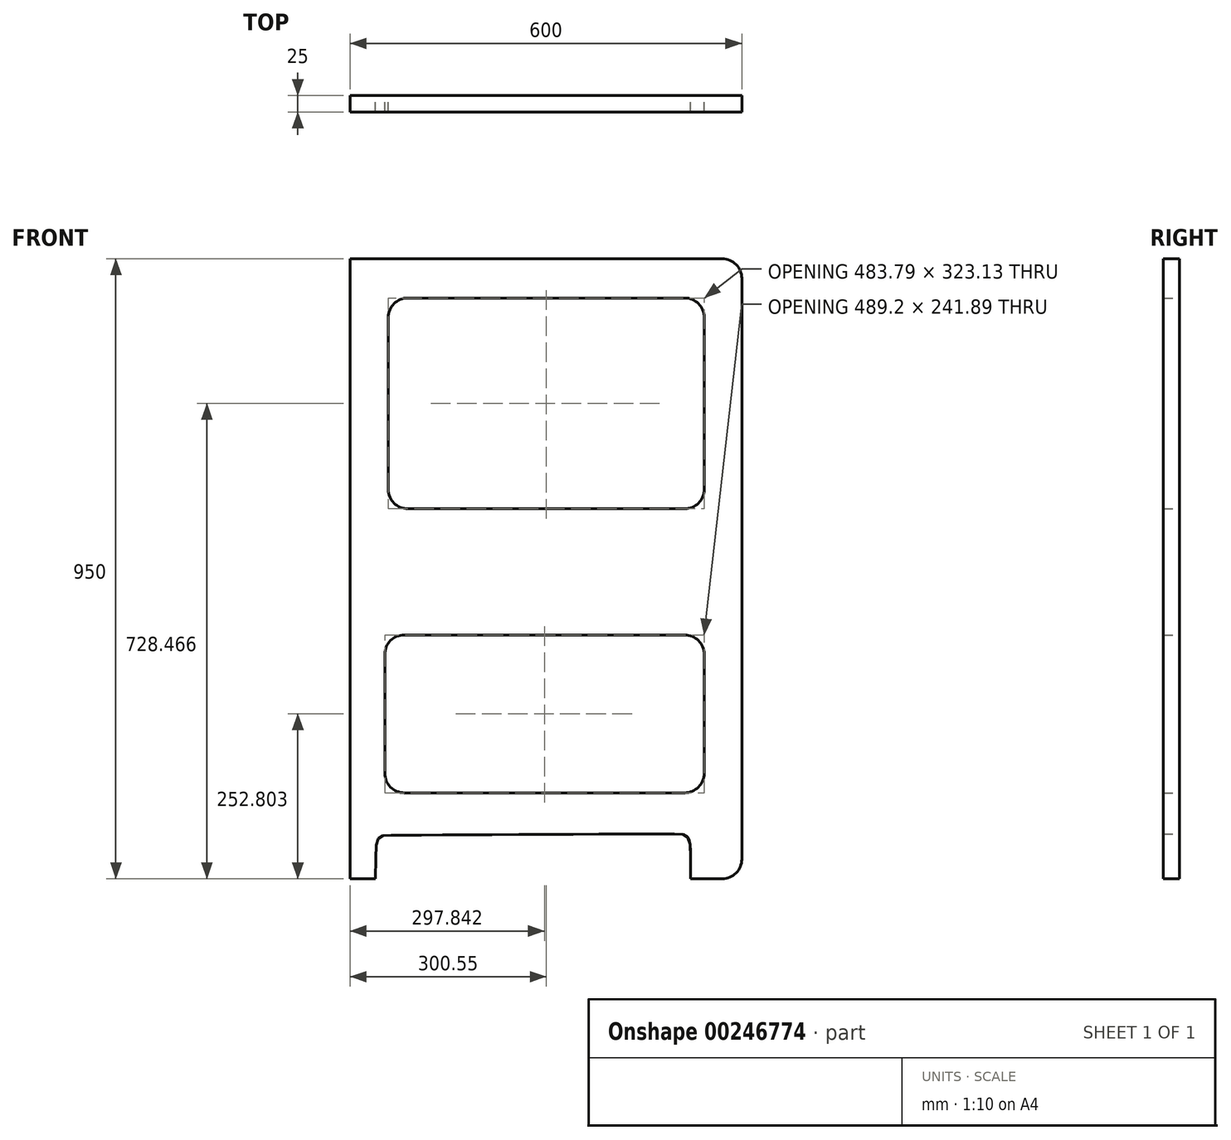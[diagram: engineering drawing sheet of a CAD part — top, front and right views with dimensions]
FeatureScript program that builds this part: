
annotation { "Feature Type Name" : "Feature", "Feature Type Description" : "" }
export const myFeature = defineFeature(function(context is Context, id is Id, definition is map)
    precondition{}
    {
        {
            var Q0;
            Q0=qCreatedBy(makeId("Front.planeOp"),FACE);
            var sketch = newSketch(context, id + "F0", { "sketchPlane" : qUnion([Q0])});
            skLineSegment(sketch, "E0.bottom", {"start": v(-370.61, 491.77) * mm, "end": v(199.39, 491.77) * mm});
            skLineSegment(sketch, "E0.top", {"start": v(-370.61, -458.23) * mm, "end": v(-331.48, -458.23) * mm});
            skLineSegment(sketch, "E0.left", {"start": v(-370.61, 491.77) * mm, "end": v(-370.61, -458.23) * mm});
            skLineSegment(sketch, "E0.right", {"start": v(229.39, 461.77) * mm, "end": v(229.39, -428.23) * mm});
            skFitSpline(sketch, "E1", {"points": [v(-331.48, -458.23) * mm, v(-304.73, -391.36) * mm, v(121.62, -389.28) * mm, v(150.81, -458.23) * mm], "startDerivative": vector(19.74, 893.3) * mm, "endDerivative": vector(0, -903.39) * mm});
            skLineSegment(sketch, "E2.trimOffspring", {"start": v(150.81, -458.23) * mm, "end": v(199.39, -458.23) * mm});
            skPoint(sketch, "E3.visualSharp", {"position": v(229.39, 491.77) * mm});
            skArc(sketch, "E3.filletArc", {"start": v(229.39, 461.77) * mm, "mid": v(220.6, 482.98) * mm, "end": v(199.39, 491.77) * mm});
            skPoint(sketch, "E4.visualSharp", {"position": v(229.39, -458.23) * mm});
            skArc(sketch, "E4.filletArc", {"start": v(199.39, -458.23) * mm, "mid": v(220.6, -449.45) * mm, "end": v(229.39, -428.23) * mm});
            skLineSegment(sketch, "E5.bottom", {"start": v(-281.95, 431.8) * mm, "end": v(141.83, 431.8) * mm});
            skLineSegment(sketch, "E5.top", {"start": v(-281.95, 108.67) * mm, "end": v(141.83, 108.67) * mm});
            skLineSegment(sketch, "E5.left", {"start": v(-311.95, 401.8) * mm, "end": v(-311.95, 138.67) * mm});
            skLineSegment(sketch, "E5.right", {"start": v(171.83, 401.8) * mm, "end": v(171.83, 138.67) * mm});
            skLineSegment(sketch, "E6.bottom", {"start": v(-287.37, -84.48) * mm, "end": v(141.83, -84.48) * mm});
            skLineSegment(sketch, "E6.top", {"start": v(-287.37, -326.37) * mm, "end": v(141.83, -326.37) * mm});
            skLineSegment(sketch, "E6.left", {"start": v(-317.37, -114.48) * mm, "end": v(-317.37, -296.37) * mm});
            skLineSegment(sketch, "E6.right", {"start": v(171.83, -114.48) * mm, "end": v(171.83, -296.37) * mm});
            skPoint(sketch, "E7.visualSharp", {"position": v(-311.95, 431.8) * mm});
            skArc(sketch, "E7.filletArc", {"start": v(-281.95, 431.8) * mm, "mid": v(-303.17, 423.01) * mm, "end": v(-311.95, 401.8) * mm});
            skPoint(sketch, "E8.visualSharp", {"position": v(171.83, 431.8) * mm});
            skArc(sketch, "E8.filletArc", {"start": v(171.83, 401.8) * mm, "mid": v(163.05, 423.01) * mm, "end": v(141.83, 431.8) * mm});
            skPoint(sketch, "E9.visualSharp", {"position": v(171.83, 108.67) * mm});
            skArc(sketch, "E9.filletArc", {"start": v(141.83, 108.67) * mm, "mid": v(163.05, 117.46) * mm, "end": v(171.83, 138.67) * mm});
            skPoint(sketch, "E10.visualSharp", {"position": v(-311.95, 108.67) * mm});
            skArc(sketch, "E10.filletArc", {"start": v(-311.95, 138.67) * mm, "mid": v(-303.17, 117.46) * mm, "end": v(-281.95, 108.67) * mm});
            skPoint(sketch, "E11.visualSharp", {"position": v(-317.37, -84.48) * mm});
            skArc(sketch, "E11.filletArc", {"start": v(-287.37, -84.48) * mm, "mid": v(-308.58, -93.27) * mm, "end": v(-317.37, -114.48) * mm});
            skPoint(sketch, "E12.visualSharp", {"position": v(171.83, -84.48) * mm});
            skArc(sketch, "E12.filletArc", {"start": v(171.83, -114.48) * mm, "mid": v(163.05, -93.27) * mm, "end": v(141.83, -84.48) * mm});
            skPoint(sketch, "E13.visualSharp", {"position": v(171.83, -326.37) * mm});
            skArc(sketch, "E13.filletArc", {"start": v(141.83, -326.37) * mm, "mid": v(163.05, -317.59) * mm, "end": v(171.83, -296.37) * mm});
            skPoint(sketch, "E14.visualSharp", {"position": v(-317.37, -326.37) * mm});
            skArc(sketch, "E14.filletArc", {"start": v(-317.37, -296.37) * mm, "mid": v(-308.58, -317.59) * mm, "end": v(-287.37, -326.37) * mm});
            skSolve(sketch);
        }
        {
            var Q0;
            Q0 = qSketchRegion(id + "F0", true);
            extrude(context, id + "F1", {"entities" : qUnion([Q0]), "depth" : 25 * mm});
        }
    });
